# Revit family: LUS-101_RFA
name_source: partatom
category: Plumbing Fixtures
units: mm (PartAtom-declared; Revit-internal decimal feet)

## family parameters
Always vertical = Yes
Cut with Voids When Loaded = No
OmniClass Number = 23.45.00.00
OmniClass Title = Sanitary, Laundry, and Cleaning Equipment
Part Type = Normal
Room Calculation Point = No
Round Connector Dimension = Use Diameter
Shared = Yes
Work Plane-Based = Yes

## types (1)
- LUS-101
    Altura Total = 11"
    Anchura Total = 2"
    Características del Producto = Monomando alto de lavabo sin contra.
    Cuerpo de Latón = Brass
    Default Elevation = 35"
    Description = Monomando alto de lavabo sin contra.
    Garantía = El producto HELVEX está garantizado como libre de defectos en materiales y procesos de fabricación. El producto HELVEX está garantizado, en lo que se refiere a los acabados; por un periodo de 10 años en los acabados cromo y duravex, y por 2 años en acabados diferentes al cromo, a partir de la fecha de compra indicada en la factura.
    Guía de Instalación = https://helvex.com.mx
    Instalación = Conexión ½ - 14 NPSM
    Manufacturer = HELVEX S.A. de C.V.
    Model = LUS-101
    Operación = Para abrir y cerrar el flujo de agua, levante y
baje el maneral.
Para regular la temperatura, gire en sentido
horario para más caliente y en sentido
antihorario para más fría.
    Presión Máxima de Trabajo = 85.3 psi
    Presión Mínima de Trabajo = 14.2 psi
    Profundidad Total = 7"
    Type Comments = Monomando alto de lavabo sin contra.

## geometry (parser evidence)
native form markers: Sweep x3
no freeform markers — native parametric forms only
